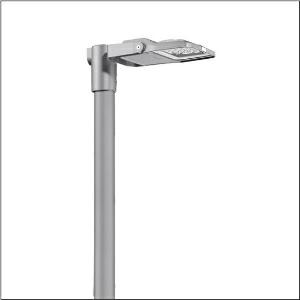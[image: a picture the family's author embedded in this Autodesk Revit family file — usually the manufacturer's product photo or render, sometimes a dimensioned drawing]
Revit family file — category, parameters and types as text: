
# Revit family: floodlight_fl_21_iq_micro___pl64_5xa7761a2e3a_b98d
name_source: partatom
category: Lighting Fixtures
units: mm (PartAtom-declared; Revit-internal decimal feet)

## family parameters
Cut with Voids When Loaded = No
Host = Face
Light Source = No
Part Type = Normal
Room Calculation Point = No
Round Connector Dimension = Use Diameter
Shared = No

## types (1)
- --- (1 x LED, 2870 lm, 23.1 W, 3000K)
    Apparent Load = 23 VA
    CIE Flux Codes = 28 80 98 100 100
    Color Rendering = 70
    Color Temperature = 3000K
    Default Elevation = 1800 mm
    Description = Floodlight FL 21 iQ micro, floodlight, primary light control with lens, of PMMA, primary optical cover: protective disc, of toughened safety glass, transparent, light distribution: PL64, light emission: direct distribution, installation type: surface-mounted, LED, High Power LED, rated luminous flux: 2.870lm, luminous efficacy: 124lm/W, light colour: 730, colour temperature: 3000K, control: optimised constant luminous flux control (CLO 2.0), Desk-Remote (wireless, voltage-free reading and setting of iQ features in the workshop via application-optimized NFC function/RFID function), Light-Fading, Smart-Wire, Night-Set, Lumen-Switch, Temp-Guard, Auto-Match, with terminal, 6-pole, mains connection: 220..240V, AC, 50/60Hz, start of lifetime: 23W, end of service life: 24W, reduction: 11W, luminaire housing, of diecast aluminium, powder-coated, Siteco® metallic grey (DB 702S), corrosivity category C5 mid according to DIN EN ISO 12944, sealing non-destructively replaceable, please order mast flange separately, mast bracket, of steel, galvanised, powder-coated, Siteco® metallic grey (DB 702S), protection rating (complete): IP66, insulation class (complete): insulation class II (safety insulation), certification: CE, ENEC, VDE, protection symbol: D, impact resistance: IK07, permissible operating ambient temperature: -40..+40°C, permissible operating ambient temperature for outdoor applications: -40..+50°C, standard: DIN EN 12944, LABS conformity tested according to VDMA 24364:2018-05, packaging unit: 1 piece

Light Distribution: PL64
    Height = 65 mm
    Lamp = 1 x LED
    Lamp Light Flux = 2870 lm
    Lamp Power = 23.1 W
    Lamp count = 1
    Length = 312 mm
    Luminous efficacy = 124 lm/W
    Manufacturer = Siteco
    ModVariant = No
    Model = 5XA7761A2E3A
    Number of Poles = 1
    OnlyDefault = Yes
    Power Factor = 1
    Product Name = Floodlight FL 21 iQ micro | PL64
    Product group = floodlight | pylon top
    ProductGroupID = 6101
    Protection Class = Protection class II
    Protection Degree = IP 66
    RLX_Detail_Level = 1
    RLX_Emergency_Light_Flux = 0 lm
    RLX_Emergency_Type = 0
    RLX_Emergency_Type_DB = No
    RlxData = <blob elided: 101665 chars, md5=ead8c524>
    Socket = socket
    Standby Power = 0 W
    System Light Flux = 2870 lm
    System Power = 23 W
    Type Comments = factory setting: luminous flux: 100 % | dim-lin: 254 | 455 mA
    Type Image = l_1007121.jpg
    URL = http://relux.com
    VarID = @adj_113935
    Voltage = 0 V
    Weight = 0.00 kg
    Width = 230 mm

## geometry (parser evidence)
native form markers: Blend x4, Sweep x12
no freeform markers — native parametric forms only
